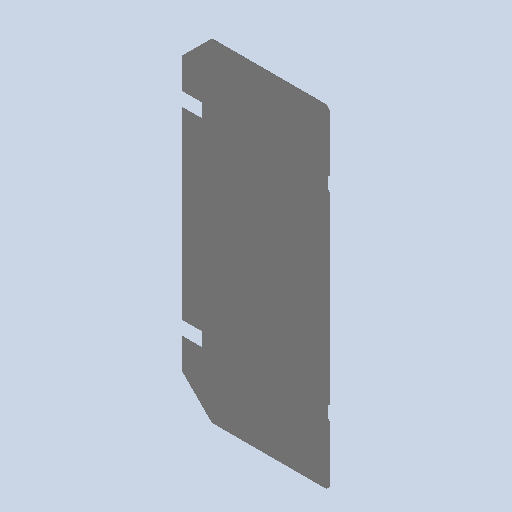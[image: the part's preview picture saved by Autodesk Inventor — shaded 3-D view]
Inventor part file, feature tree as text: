
AUTODESK INVENTOR PART (.ipt)
format: ipt  version: 2022.1 (Build 261234000, 234)  size: 156,160 bytes
history: native  units: mm
features: reference x12, other x9, sheet_metal_op x1, chamfer x1, sketch x1
ambient origin geometry x8: Origin, YZ Plane, XZ Plane, XY Plane, X Axis, Y Axis, Z Axis, Center Point
bodies: Solid1 (feature_tree)
feature tree (24):
  sheet_metal_op  "Face1"
  chamfer  "Corner Round1"
  sketch  "Sketch1"  dims[d1=1.0mm d2=1.0mm d3=1.0mm d4=1.0mm d5=1.0mm d6=1.0mm d7=1.0mm d10=1.0mm d15=1.0mm d16=0.5mm d17=4.0mm d18=1.0mm d19=1.0mm d20=1.0mm d21=1.0mm d22=1.0mm d24=1.0mm]
  reference  "Reference1"
  reference  "Reference2"
  reference  "Reference3"
  reference  "Reference4"
  reference  "Reference5"
  reference  "Reference6"
  other  "Plate1"
  reference  "Reference7"
  reference  "Reference8"
  reference  "Reference9"
  reference  "Reference10"
  reference  "Reference11"
  reference  "Reference12"
  other  "RobotPallet.iam"
  other  "EstructuraInferior:1"
  other  "Frame_Base:1"
  other  "ISO 10799-2 40x40x2 - 2899.41:1"
  other  "ISO 10799-2 40x40x2 - 444:1"
  other  "ISO 10799-2 40x40x2 - 211.1:2"
  other  "ISO 10799-2 40x40x2 - 211.1:1"
  other  "ISO 10799-2 40x40x2 - 464:2"
